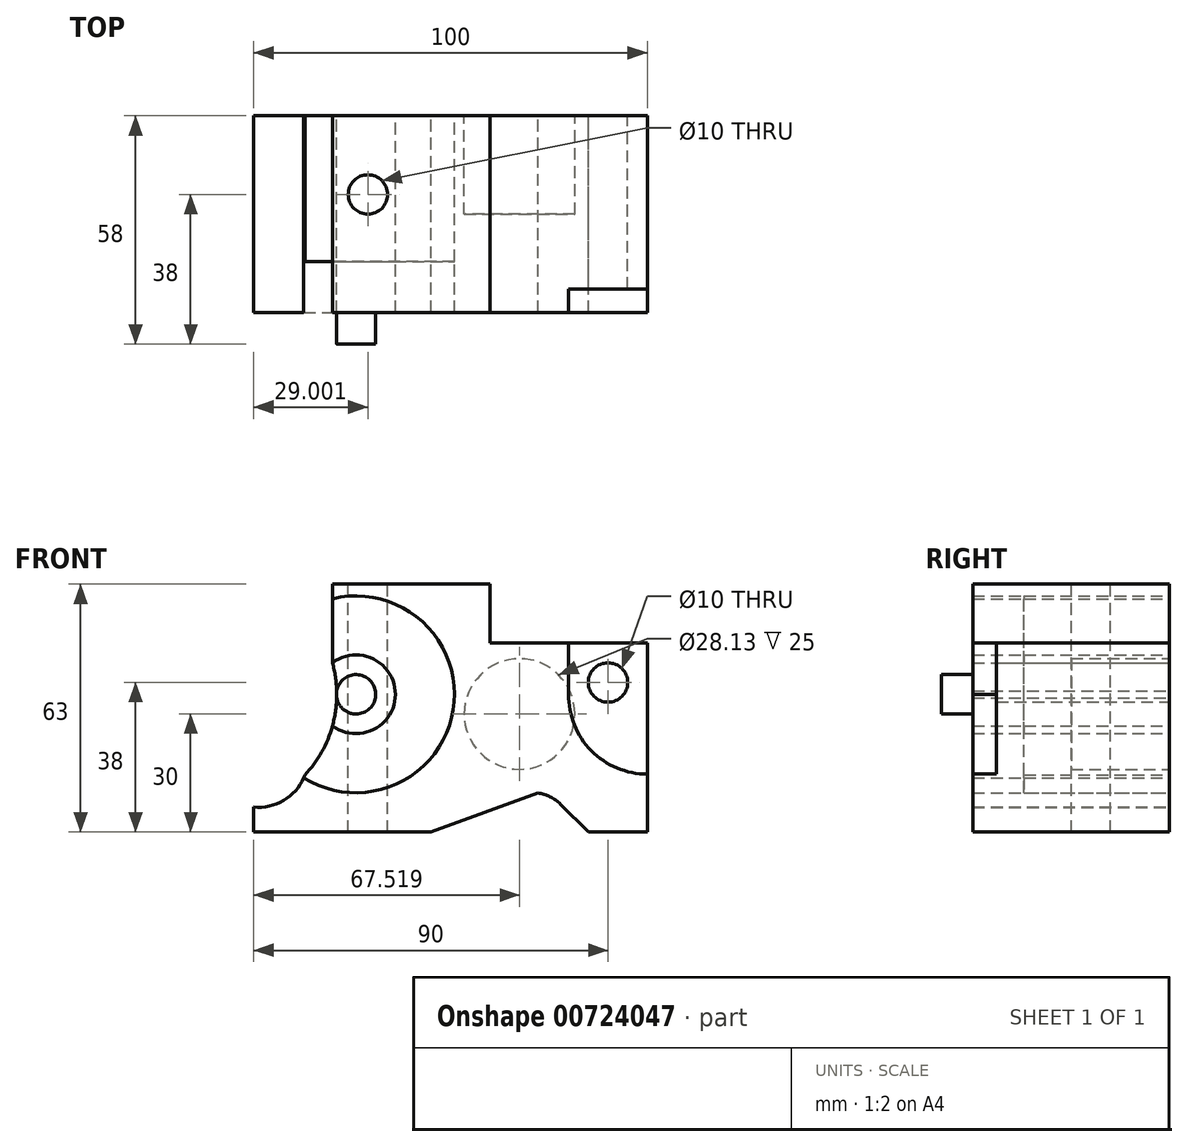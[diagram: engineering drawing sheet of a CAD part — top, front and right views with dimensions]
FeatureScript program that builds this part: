
annotation { "Feature Type Name" : "Feature", "Feature Type Description" : "" }
export const myFeature = defineFeature(function(context is Context, id is Id, definition is map)
    precondition{}
    {
        {
            var Q0;
            Q0=qCreatedBy(makeId("Front.planeOp"),FACE);
            var sketch = newSketch(context, id + "F0", { "sketchPlane" : qUnion([Q0])});
            skLineSegment(sketch, "E0", {"start": v(0, 0) * mm, "end": v(0, 48) * mm});
            skLineSegment(sketch, "E1", {"start": v(0, 48) * mm, "end": v(-40, 48) * mm});
            skLineSegment(sketch, "E2", {"start": v(-40, 48) * mm, "end": v(-40, 63) * mm});
            skLineSegment(sketch, "E3", {"start": v(-40, 63) * mm, "end": v(-80, 63) * mm});
            skArc(sketch, "E4", {"start": v(-87.28, 13.82) * mm, "mid": v(-49.31, 31.04) * mm, "end": v(-80, 59.27) * mm});
            skLineSegment(sketch, "E5", {"start": v(-100, 6.35) * mm, "end": v(-100, 0) * mm});
            skLineSegment(sketch, "E6", {"start": v(-100, 0) * mm, "end": v(-55, 0) * mm});
            skLineSegment(sketch, "E7", {"start": v(-55, 0) * mm, "end": v(-27.78, 9.9) * mm});
            skLineSegment(sketch, "E8", {"start": v(-15, 0) * mm, "end": v(0, 0) * mm});
            skArc(sketch, "E9", {"start": v(-22.07, 7.07) * mm, "mid": v(-24.7, 8.96) * mm, "end": v(-27.78, 9.9) * mm});
            skLineSegment(sketch, "E10", {"start": v(-15, 0) * mm, "end": v(-22.07, 7.07) * mm});
            skCircle(sketch, "E11", {"center": v(-74, 35) * mm, "radius": 5 * mm});
            skCircle(sketch, "E12", {"center": v(-10, 38) * mm, "radius": 5 * mm});
            skPoint(sketch, "E13.centerSnap0", {"position": v(0, 24) * mm});
            skLineSegment(sketch, "E14", {"start": v(-20, 35) * mm, "end": v(-20, 48) * mm});
            skArc(sketch, "E15.trimOffspring", {"start": v(-20, 35) * mm, "mid": v(-14.24, 20.68) * mm, "end": v(0, 14.72) * mm});
            skPoint(sketch, "E13.center.orphan", {"position": v(0, 24) * mm});
            skPoint(sketch, "E16.end.orphan", {"position": v(-85.47, 57.21) * mm});
            skLineSegment(sketch, "E17", {"start": v(-80, 43) * mm, "end": v(-80, 63) * mm});
            skPoint(sketch, "E18.orphan", {"position": v(-81.47, 63) * mm});
            skArc(sketch, "E19", {"start": v(-80, 27) * mm, "mid": v(-64, 35) * mm, "end": v(-80, 43) * mm});
            skArc(sketch, "E20", {"start": v(-87.01, 14.5) * mm, "mid": v(-79.78, 27.83) * mm, "end": v(-80, 43) * mm});
            skArc(sketch, "E21", {"start": v(-100, 6.35) * mm, "mid": v(-92.42, 8.01) * mm, "end": v(-87.28, 13.82) * mm});
            skLineSegment(sketch, "E22", {"start": v(-87.28, 13.82) * mm, "end": v(-87.01, 14.5) * mm});
            skSolve(sketch);
        }
        {
            var Q0;
            {var subQ0=sQuery(id+"F0.wireOp",EDGE,"E21");var subQ1=sQuery(id+"F0.wireOp",EDGE,"E4");var subQ2=makeQuery(id+"F0.imprint","INTERSECT",VERTEX,{"derivedFrom":[subQ1,subQ0]});Q0=makeQuery(id+"F0.imprint","IMPRINT",FACE,{"disambiguationData":[TD([[makeQuery(id+"F0.imprint","IMPRINT",EDGE,{"disambiguationData":[TD([[subQ2,-1.0]])],"derivedFrom":subQ1}),-1.0]])]});}
            var Q1;
            {var subQ0=sQuery(id+"F0.wireOp",EDGE,"E20");var subQ1=sQuery(id+"F0.wireOp",EDGE,"E19");var subQ3=makeQuery(id+"F0.imprint","INTERSECT",VERTEX,{"derivedFrom":[subQ1,subQ0]});Q1=makeQuery(id+"F0.imprint","IMPRINT",FACE,{"disambiguationData":[TD([[makeQuery(id+"F0.imprint","IMPRINT",EDGE,{"disambiguationData":[TD([[subQ3,1.0]])],"derivedFrom":subQ1}),1.0]])]});}
            var Q2;
            {var subQ10=sQuery(id+"F0.wireOp",EDGE,"E2");Q2=makeQuery(id+"F0.imprint","IMPRINT",FACE,{"disambiguationData":[TD([[makeQuery(id+"F0.imprint","IMPRINT",EDGE,{"derivedFrom":subQ10}),1.0]])]});}
            extrude(context, id + "F1", {"entities" : qUnion([Q0, Q1, Q2]), "depth" : 50 * mm, "offsetDistance" : 25 * mm});
        }
        {
            var Q0;
            {var subQ0=sQuery(id+"F0.wireOp",EDGE,"E17");var subQ1=sQuery(id+"F0.wireOp",EDGE,"E4");var subQ2=makeQuery(id+"F0.imprint","INTERSECT",VERTEX,{"derivedFrom":[subQ1,subQ0]});Q0=makeQuery(id+"F0.imprint","IMPRINT",FACE,{"disambiguationData":[TD([[makeQuery(id+"F0.imprint","IMPRINT",EDGE,{"disambiguationData":[TD([[subQ2,1.0]])],"derivedFrom":subQ1}),1.0]])]});}
            extrude(context, id + "F2", {"entities" : qUnion([Q0]), "operationType" : NewBodyOperationType.ADD, "depth" : (50 - 13) * mm, "offsetDistance" : 25 * mm});
        }
        {
            var Q0;
            Q0=makeQuery(id+"F0.imprint","IMPRINT",FACE,{"disambiguationData":[TD([[makeQuery(id+"F0.imprint","IMPRINT",EDGE,{"derivedFrom":sQuery(id+"F0.wireOp",EDGE,"E11")}),-1.0]])]});
            extrude(context, id + "F3", {"entities" : qUnion([Q0]), "depth" : (50 - 8) * mm, "offsetDistance" : 25 * mm});
        }
        {
            var Q0;
            Q0=makeQuery(id+"F0.imprint","IMPRINT",FACE,{"disambiguationData":[TD([[makeQuery(id+"F0.imprint","IMPRINT",EDGE,{"derivedFrom":sQuery(id+"F0.wireOp",EDGE,"E11")}),1.0]])]});
            extrude(context, id + "F4", {"entities" : qUnion([Q0]), "operationType" : NewBodyOperationType.ADD, "depth" : 58 * mm, "offsetDistance" : 25 * mm});
        }
        {
            var Q0;
            Q0=makeQuery(id+"F0.imprint","IMPRINT",FACE,{"disambiguationData":[TD([[makeQuery(id+"F0.imprint","IMPRINT",EDGE,{"derivedFrom":sQuery(id+"F0.wireOp",EDGE,"E12")}),-1.0]])]});
            extrude(context, id + "F5", {"entities" : qUnion([Q0]), "operationType" : NewBodyOperationType.ADD, "depth" : (50 - 6) * mm, "offsetDistance" : 25 * mm});
        }
        {
            var Q0;
            Q0=makeQuery(id+"F1.opExtrude","SWEPT_FACE",FACE,{"disambiguationData":[OSD([sQuery(id+"F0.wireOp",EDGE,"E3")])]});
            var sketch = newSketch(context, id + "F6", { "sketchPlane" : qUnion([Q0])});
            skCircle(sketch, "E23", {"center": v(-71, -20) * mm, "radius": 5 * mm});
            skSolve(sketch);
        }
        {
            var Q0;
            Q0=makeQuery(id+"F6.imprint","IMPRINT",FACE,{"disambiguationData":[TD([[makeQuery(id+"F6.imprint","IMPRINT",EDGE,{"derivedFrom":sQuery(id+"F6.wireOp",EDGE,"E23")}),1.0]])]});
            extrude(context, id + "F7", {"entities" : qUnion([Q0]), "operationType" : NewBodyOperationType.REMOVE, "endBound" : BoundingType.THROUGH_ALL, "oppositeDirection" : true, "depth" : 10 * mm, "offsetDistance" : 25 * mm});
        }
        {
            var Q0;
            {var subQ2=sQuery(id+"F0.wireOp",EDGE,"E4");Q0=makeQuery(id+"F0.imprint","IMPRINT",FACE,{"disambiguationData":[TD([[makeQuery(id+"F0.imprint","IMPRINT",EDGE,{"derivedFrom":subQ2}),1.0]])]});}
            extrude(context, id + "F8", {"entities" : qUnion([Q0]), "depth" : (50 - 13) * mm, "offsetDistance" : 25 * mm});
        }
        {
            var Q0;
            {var subQ0=sQuery(id+"F0.wireOp",EDGE,"E15.trimOffspring");var subQ1=sQuery(id+"F0.wireOp",EDGE,"E14");var subQ2=sQuery(id+"F0.wireOp",EDGE,"E1");var subQ3=sQuery(id+"F0.wireOp",EDGE,"E0");var subQ4=sQuery(id+"F0.wireOp",EDGE,"E17");var subQ5=sQuery(id+"F0.wireOp",EDGE,"E4");Q0=makeQuery(id+"F5.boolean.opBoolean","MERGE",FACE,{"derivedFrom":[makeQuery(id+"F2.boolean.opBoolean","MERGE",FACE,{"derivedFrom":[makeQuery(id+"F1.opExtrude","CAP_FACE",FACE,{"disambiguationData":[OSD([subQ3,subQ2,sQuery(id+"F0.wireOp",EDGE,"E2"),sQuery(id+"F0.wireOp",EDGE,"E3"),subQ5,sQuery(id+"F0.wireOp",EDGE,"E5"),sQuery(id+"F0.wireOp",EDGE,"E6"),sQuery(id+"F0.wireOp",EDGE,"E7"),sQuery(id+"F0.wireOp",EDGE,"E8"),sQuery(id+"F0.wireOp",EDGE,"E9"),sQuery(id+"F0.wireOp",EDGE,"E10"),subQ1,subQ0,subQ4,sQuery(id+"F0.wireOp",EDGE,"E21")])],"isStart":true}),makeQuery(id+"F2.opExtrude","CAP_FACE",FACE,{"disambiguationData":[OSD([subQ5,subQ4,sQuery(id+"F0.wireOp",EDGE,"E19"),sQuery(id+"F0.wireOp",EDGE,"E20"),sQuery(id+"F0.wireOp",EDGE,"E22")])],"isStart":true})]}),makeQuery(id+"F5.opExtrude","CAP_FACE",FACE,{"disambiguationData":[OSD([subQ3,subQ2,sQuery(id+"F0.wireOp",EDGE,"E12"),subQ1,subQ0])],"isStart":true})]});}
            var sketch = newSketch(context, id + "F9", { "sketchPlane" : qUnion([Q0])});
            skCircle(sketch, "E24", {"center": v(32.48, 30) * mm, "radius": 14.06 * mm});
            skSolve(sketch);
        }
        {
            var Q0;
            Q0=makeQuery(id+"F9.imprint","IMPRINT",FACE,{"disambiguationData":[TD([[makeQuery(id+"F9.imprint","IMPRINT",EDGE,{"derivedFrom":sQuery(id+"F9.wireOp",EDGE,"E24")}),1.0]])]});
            extrude(context, id + "F10", {"entities" : qUnion([Q0]), "operationType" : NewBodyOperationType.REMOVE, "oppositeDirection" : true, "depth" : 25 * mm, "offsetDistance" : 25 * mm});
        }
    });
